# Revit family: Gewindeplatte Vierkant VA
name_source: partatom
category: HLS-Bauteile
revit_build: Autodesk Revit 2017 (Build: 20190507_1515(x64)
units: mm (PartAtom-declared; Revit-internal decimal feet)

## family parameters
Arbeitsebenenbasiert = Ja
Beim Laden mit Abzugskörper schneiden = Nein
Bemaßung runder Anschluss = Durchmesser verwenden
Gemeinsam genutzt = Ja
Immer vertikal = Nein
Raumberechnungspunkt = Nein
Teiletyp = Normal

## types (14) — shared parameters
Anzugsmoment = 0.00 kN-m
Fabrikat = MEFA
Firma = MEFA Befestigungs- und Montagesysteme GmbH
Form = vierkant
Material = Edelstahl
Mengeneinheit = St
Profil = C-Profil
Vorgabe-Ansicht = 1219 mm

## per-type parameters (varying)
| type | Abmessung | Artikelnummer | B | Breite | EAN | Gewicht | Gewicht pro Bauteil | Gewinde | Kurztext1 | Kurztext2 | L | Länge | Profiltyp | S | Schienenbreite | Stärke Material | d2 | vpe |
| Gewindeplatte Vierkant 35x 30x 5 M 8 V4A | 35 x 30 x 5 mm | 0481611 | 30 mm  [stored 0.0984252 ft] | 30 mm  [stored 0.0984252 ft] | 4250928413048 | 0.04 kg | 0.04 kg | M8 | Gewindeplatte V4A | M8 vierkant 35 x 30 mm | 35 mm  [stored 0.114829 ft] | 35 mm  [stored 0.114829 ft] | 35, 45 | 5 mm  [stored 0.0164042 ft] | 45 mm | 5 mm  [stored 0.0164042 ft] | 4 mm  [stored 0.0131234 ft] | 50 St |
| Gewindeplatte Vierkant 35x 30x 6 M10 V4A | 35 x 30 x 6 mm | 0481612 | 30 mm  [stored 0.0984252 ft] | 30 mm  [stored 0.0984252 ft] | 4250928413055 | 0.05 kg | 0.05 kg | M10 | Gewindeplatte V4A | M10 vierkant 35 x 30 mm | 35 mm  [stored 0.114829 ft] | 35 mm  [stored 0.114829 ft] | 35, 45 | 6 mm  [stored 0.019685 ft] | 45 mm | 6 mm  [stored 0.019685 ft] | 5 mm  [stored 0.0164042 ft] | 50 St |
| Gewindeplatte Vierkant 35x 30x 6 M12 V4A | 35 x 30 x 6 mm | 0481613 | 30 mm  [stored 0.0984252 ft] | 30 mm  [stored 0.0984252 ft] | 4250928413062 | 0.05 kg | 0.05 kg | M12 | Gewindeplatte V4A | M12 vierkant 35 x 30 mm | 35 mm  [stored 0.114829 ft] | 35 mm  [stored 0.114829 ft] | 35, 45 | 6 mm  [stored 0.019685 ft] | 45 mm | 6 mm  [stored 0.019685 ft] | 6 mm  [stored 0.019685 ft] | 50 St |
| Gewindeplatte Vierkant 35x 30x 6 M16 V4A | 35 x 30 x 6 mm | 0481614 | 30 mm  [stored 0.0984252 ft] | 30 mm  [stored 0.0984252 ft] | 4250928413079 | 0.04 kg | 0.04 kg | M16 | Gewindeplatte V4A | M16 vierkant 35 x 30 mm | 35 mm  [stored 0.114829 ft] | 35 mm  [stored 0.114829 ft] | 35, 45 | 6 mm  [stored 0.019685 ft] | 45 mm | 6 mm  [stored 0.019685 ft] | 8 mm  [stored 0.0262467 ft] | 50 St |
| Gewindeplatte Vierkant 35x 30x 5 M 8 V2A | 35 x 30 x 5 mm | 0480611 | 30 mm  [stored 0.0984252 ft] | 30 mm  [stored 0.0984252 ft] | 4250928412720 | 0.04 kg | 0.04 kg | M8 | Gewindeplatte V2A | M8 vierkant 35 x 30 mm | 35 mm  [stored 0.114829 ft] | 35 mm  [stored 0.114829 ft] | 35, 45 | 5 mm  [stored 0.0164042 ft] | 35, 45 mm | 5 mm  [stored 0.0164042 ft] | 4 mm  [stored 0.0131234 ft] | 50 St |
| Gewindeplatte Vierkant 35x 30x 6 M10 V2A | 35 x 30 x 6 mm | 0480612 | 30 mm  [stored 0.0984252 ft] | 30 mm  [stored 0.0984252 ft] | 4250928412737 | 0.05 kg | 0.05 kg | M10 | Gewindeplatte V2A | M10 vierkant 35 x 30 mm | 35 mm  [stored 0.114829 ft] | 35 mm  [stored 0.114829 ft] | 35, 45 | 6 mm  [stored 0.019685 ft] | 35, 45 mm | 6 mm  [stored 0.019685 ft] | 5 mm  [stored 0.0164042 ft] | 50 St |
| Gewindeplatte Vierkant 35x 30x 6 M12 V2A | 35 x 30 x 6 mm | 0480613 | 30 mm  [stored 0.0984252 ft] | 30 mm  [stored 0.0984252 ft] | 4250928412744 | 0.05 kg | 0.05 kg | M12 | Gewindeplatte V2A | M12 vierkant 35 x 30 mm | 35 mm  [stored 0.114829 ft] | 35 mm  [stored 0.114829 ft] | 35, 45 | 6 mm  [stored 0.019685 ft] | 35, 45 mm | 6 mm  [stored 0.019685 ft] | 6 mm  [stored 0.019685 ft] | 50 St |
| Gewindeplatte Vierkant 35x 30x 6 M16 V2A | 35 x 30 x 6 mm | 0480614 | 30 mm  [stored 0.0984252 ft] | 30 mm  [stored 0.0984252 ft] | 4250928412751 | 0.04 kg | 0.04 kg | M16 | Gewindeplatte V2A | M16 vierkant 35 x 30 mm | 35 mm  [stored 0.114829 ft] | 35 mm  [stored 0.114829 ft] | 35, 45 | 6 mm  [stored 0.019685 ft] | 35, 45 mm | 6 mm  [stored 0.019685 ft] | 8 mm  [stored 0.0262467 ft] | 50 St |
| Gewindeplatte Vierkant 30x 22x 5 M 8 V2A | 30 x 22 x 5 mm | 0750818 | 22 mm  [stored 0.0721785 ft] | 22 mm  [stored 0.0721785 ft] | 4250928417282 | 0.03 kg | 0.03 kg | M8 | Gewindeplatte V2A | M8 vierkant 30 x 22 mm | 30 mm  [stored 0.0984252 ft] | 30 mm  [stored 0.0984252 ft] | 27, 35 | 5 mm  [stored 0.0164042 ft] | 27, 35 mm | 5 mm  [stored 0.0164042 ft] | 4 mm  [stored 0.0131234 ft] | 100 St |
| Gewindeplatte Vierkant 30x 22x 5 M 8 V4A | 30 x 22 x 5 mm | 0750838 | 22 mm  [stored 0.0721785 ft] | 22 mm  [stored 0.0721785 ft] | 4250928417312 | 0.03 kg | 0.03 kg | M8 | Gewindeplatte V4A | M8 vierkant 30 x 22 mm | 30 mm  [stored 0.0984252 ft] | 30 mm  [stored 0.0984252 ft] | 27, 35 | 5 mm  [stored 0.0164042 ft] | 35 mm | 5 mm  [stored 0.0164042 ft] | 4 mm  [stored 0.0131234 ft] | 100 St |
| Gewindeplatte Vierkant 30x 22x 5 M10 V2A | 30 x 22 x 5 mm | 0750820 | 22 mm  [stored 0.0721785 ft] | 22 mm  [stored 0.0721785 ft] | 4250928417299 | 0.02 kg | 0.02 kg | M10 | Gewindeplatte V2A | M10 vierkant 30 x 22 mm | 30 mm  [stored 0.0984252 ft] | 30 mm  [stored 0.0984252 ft] | 27, 35 | 5 mm  [stored 0.0164042 ft] | 27, 35 mm | 5 mm  [stored 0.0164042 ft] | 5 mm  [stored 0.0164042 ft] | 100 St |
| Gewindeplatte Vierkant 30x 22x 5 M12 V2A | 30 x 22 x 5 mm | 0750822 | 22 mm  [stored 0.0721785 ft] | 22 mm  [stored 0.0721785 ft] | 4250928417305 | 0.02 kg | 0.02 kg | M12 | Gewindeplatte V2A | M12 vierkant 30 x 22 mm | 30 mm  [stored 0.0984252 ft] | 30 mm  [stored 0.0984252 ft] | 27, 35 | 5 mm  [stored 0.0164042 ft] | 27, 35 mm | 5 mm  [stored 0.0164042 ft] | 6 mm  [stored 0.019685 ft] | 100 St |
| Gewindeplatte Vierkant 30x 22x 5 M10 V4A | 30 x 22 x 5 mm | 0750840 | 22 mm  [stored 0.0721785 ft] | 22 mm  [stored 0.0721785 ft] | 4250928417329 | 0.02 kg | 0.02 kg | M10 | Gewindeplatte V4A | M10 vierkant 30 x 22 mm | 30 mm  [stored 0.0984252 ft] | 30 mm  [stored 0.0984252 ft] | 27, 35 | 5 mm  [stored 0.0164042 ft] | 35 mm | 5 mm  [stored 0.0164042 ft] | 5 mm  [stored 0.0164042 ft] | 100 St |
| Gewindeplatte Vierkant 30x 22x 5 M12 V4A | 30 x 22 x 5 mm | 0750842 | 22 mm  [stored 0.0721785 ft] | 22 mm  [stored 0.0721785 ft] | 4250928417336 | 0.02 kg | 0.02 kg | M12 | Gewindeplatte V4A | M12 vierkant 30 x 22 mm | 30 mm  [stored 0.0984252 ft] | 30 mm  [stored 0.0984252 ft] | 27, 35 | 5 mm  [stored 0.0164042 ft] | 35 mm | 5 mm  [stored 0.0164042 ft] | 6 mm  [stored 0.019685 ft] | 100 St |

note: [stored X ft] marks values corroborated as IEEE doubles in the binary element streams (Revit-internal decimal feet)
